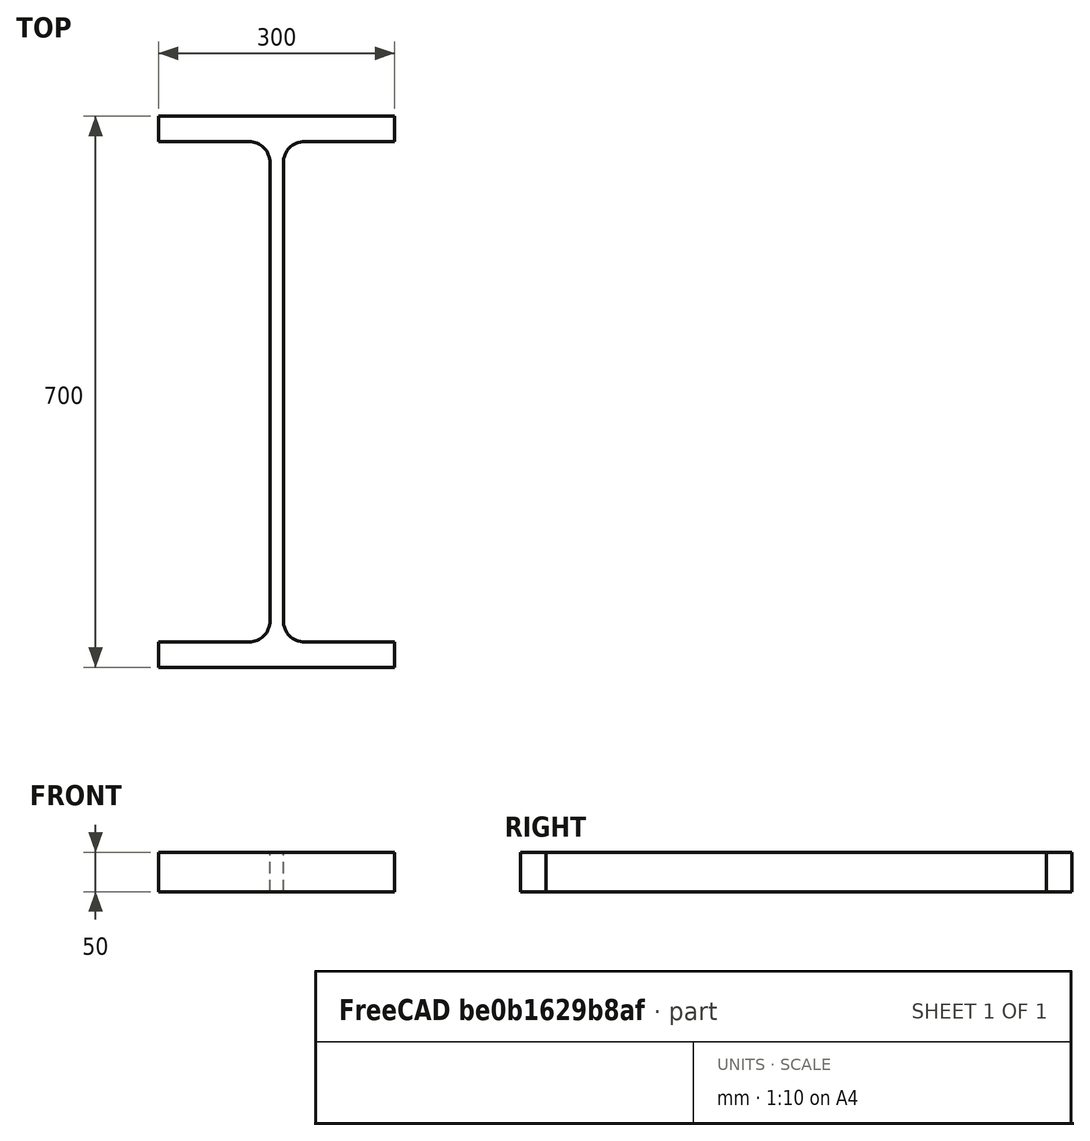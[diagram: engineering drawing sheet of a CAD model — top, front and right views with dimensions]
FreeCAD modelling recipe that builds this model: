
FCSTD DOCUMENT  (FreeCAD 0.15R4671 (Git))
Label: HE-B-Profile 700 DIN1025-2 S235JR
License: All rights reserved
LicenseURL: http://en.wikipedia.org/wiki/All_rights_reserved
objects: Sketcher::SketchObject×1, Part::Extrusion×1
note: 2 computed .brp shape members not serialized (recipe doc carries the construction recipe); baked Part::Feature solids carry a one-line shape summary decoded from their .brp

FEATURE [Sketcher::SketchObject] Sketch
  sketch-geometry (16):
    g0: LineSegment StartX=8.5 StartY=-291 StartZ=0 EndX=8.5 EndY=291 EndZ=0
    g1: LineSegment StartX=35.5 StartY=318 StartZ=0 EndX=150 EndY=318 EndZ=0
    g2: LineSegment StartX=150 StartY=318 StartZ=0 EndX=150 EndY=350 EndZ=0
    g3: LineSegment StartX=150 StartY=350 StartZ=0 EndX=-150 EndY=350 EndZ=0
    g4: LineSegment StartX=-150 StartY=350 StartZ=0 EndX=-150 EndY=318 EndZ=0
    g5: LineSegment StartX=-150 StartY=318 StartZ=0 EndX=-35.5 EndY=318 EndZ=0
    g6: LineSegment StartX=-8.5 StartY=291 StartZ=0 EndX=-8.5 EndY=-291 EndZ=0
    g7: LineSegment StartX=-35.5 StartY=-318 StartZ=0 EndX=-150 EndY=-318 EndZ=0
    g8: LineSegment StartX=-150 StartY=-318 StartZ=0 EndX=-150 EndY=-350 EndZ=0
    g9: LineSegment StartX=-150 StartY=-350 StartZ=0 EndX=150 EndY=-350 EndZ=0
    g10: LineSegment StartX=150 StartY=-350 StartZ=0 EndX=150 EndY=-318 EndZ=0
    g11: LineSegment StartX=150 StartY=-318 StartZ=0 EndX=35.5 EndY=-318 EndZ=0
    g12: ArcOfCircle CenterX=35.5 CenterY=291 CenterZ=0 NormalX=0 NormalY=0 NormalZ=1 Radius=27 StartAngle=1.5708 EndAngle=3.14159
    g13: ArcOfCircle CenterX=35.5 CenterY=-291 CenterZ=0 NormalX=0 NormalY=0 NormalZ=1 Radius=27 StartAngle=3.14159 EndAngle=4.71239
    g14: ArcOfCircle CenterX=-35.5 CenterY=291 CenterZ=0 NormalX=0 NormalY=0 NormalZ=1 Radius=27 StartAngle=0 EndAngle=1.5708
    g15: ArcOfCircle CenterX=-35.5 CenterY=-291 CenterZ=0 NormalX=0 NormalY=0 NormalZ=1 Radius=27 StartAngle=4.71239 EndAngle=6.28319
  constraints (42):
    c: Vertical(g0)
    c: Coincident(g2,g1)
    c: Vertical(g2)
    c: Coincident(g3,g2)
    c: Coincident(g4,g3)
    c: Vertical(g4)
    c: Coincident(g5,g4)
    c: Horizontal(g5)
    c: Vertical(g6)
    c: Horizontal(g7)
    c: Coincident(g8,g7)
    c: Vertical(g8)
    c: Coincident(g9,g8)
    c: Horizontal(g9)
    c: Coincident(g10,g9)
    c: Vertical(g10)
    c: Coincident(g11,g10)
    c: Horizontal(g11)
    c: Tangent(g1,g12) = 1.5708
    c: Tangent(g0,g12) = 1.5708
    c: Tangent(g0,g13) = 1.5708
    c: Tangent(g11,g13) = 1.5708
    c: Tangent(g5,g14) = 1.5708
    c: Tangent(g6,g14) = 1.5708
    c: Tangent(g6,g15) = 1.5708
    c: Tangent(g7,g15) = 1.5708
    c: Equal(g3,g9)
    c: Equal(g2,g4)
    c: Equal(g4,g8)
    c: Equal(g8,g10)
    c: Equal(g12,g14)
    c: Equal(g14,g15)
    c: Equal(g15,g13)
    c: Symmetric(g2,g3,g-2)
    c: Symmetric(g9,g8,g-2)
    c: Symmetric(g0,g6,g-2)
    c: Symmetric(g2,g9,g-1)
    c: DistanceY(g2,g9) = -700
    c: DistanceX(g3) = -300
    c: DistanceX(g0,g6) = -17
    c: DistanceY(g2) = 32
    c: Radius(g12) = 27
FEATURE [Part::Extrusion] Extrude  label="HE-B-Profile 700 DIN1025-2 S235JR"
  Base = -> Sketch
  Dir = (0,0,50)
  Solid = true
